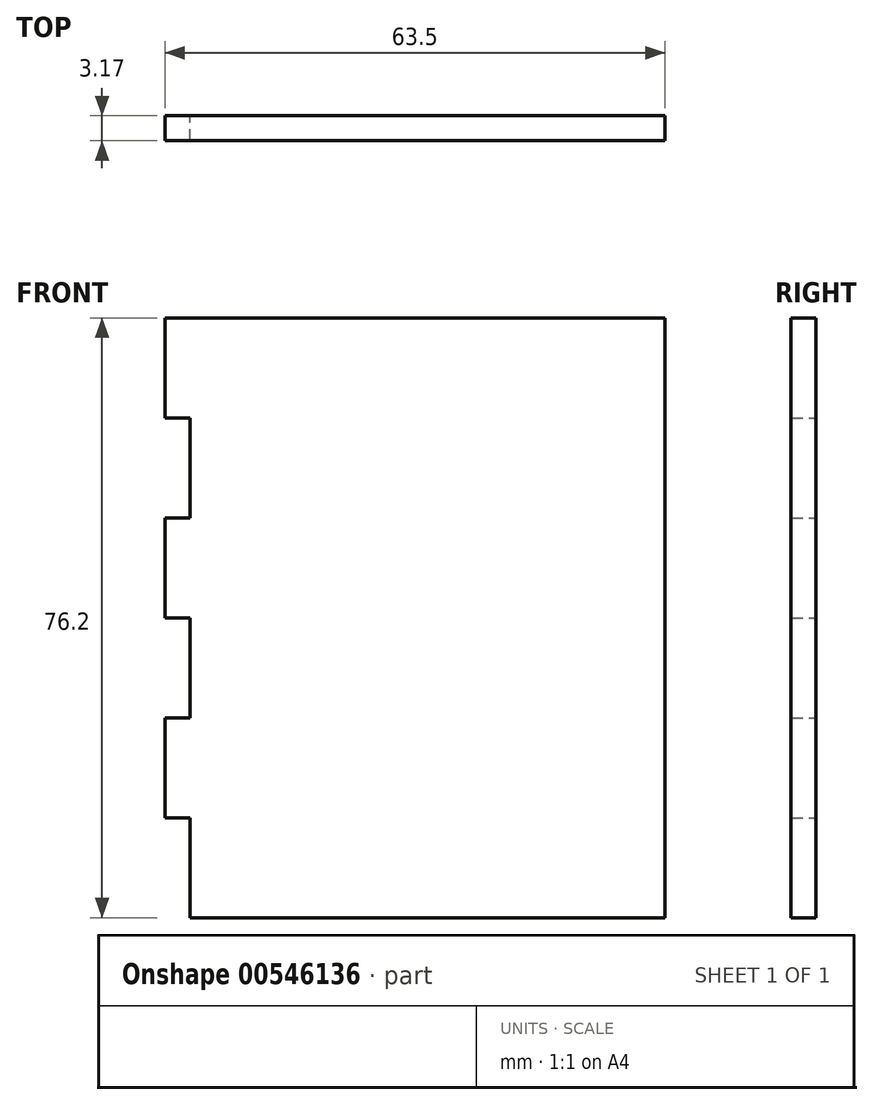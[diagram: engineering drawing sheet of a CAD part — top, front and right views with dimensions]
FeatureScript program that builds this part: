
annotation { "Feature Type Name" : "Feature", "Feature Type Description" : "" }
export const myFeature = defineFeature(function(context is Context, id is Id, definition is map)
    precondition{}
    {
        {
            var Q0;
            Q0=qCreatedBy(makeId("Front.planeOp"),FACE);
            var sketch = newSketch(context, id + "F0", { "sketchPlane" : qUnion([Q0])});
            skLineSegment(sketch, "E0.bottom", {"start": v(31.75, -38.1) * mm, "end": v(-31.75, -38.1) * mm});
            skLineSegment(sketch, "E0.top", {"start": v(31.75, 38.1) * mm, "end": v(-31.75, 38.1) * mm});
            skLineSegment(sketch, "E0.left", {"start": v(31.75, -38.1) * mm, "end": v(31.75, 38.1) * mm});
            skLineSegment(sketch, "E0.right", {"start": v(-31.75, -38.1) * mm, "end": v(-31.75, 38.1) * mm});
            skPoint(sketch, "E0.middle", {"position": v(0, 0) * mm});
            skSolve(sketch);
        }
        {
            var Q0;
            Q0 = qSketchRegion(id + "F0", true);
            extrude(context, id + "F1", {"entities" : qUnion([Q0]), "depth" : 3.17 * mm, "offsetDistance" : 25.4 * mm});
        }
        {
            var Q0;
            Q0=qCreatedBy(makeId("Front.planeOp"),FACE);
            var sketch = newSketch(context, id + "F2", { "sketchPlane" : qUnion([Q0])});
            skLineSegment(sketch, "E1.bottom", {"start": v(-31.75, 25.4) * mm, "end": v(-28.57, 25.4) * mm});
            skLineSegment(sketch, "E1.top", {"start": v(-31.75, 12.7) * mm, "end": v(-28.57, 12.7) * mm});
            skLineSegment(sketch, "E1.left", {"start": v(-31.75, 25.4) * mm, "end": v(-31.75, 12.7) * mm});
            skLineSegment(sketch, "E1.right", {"start": v(-28.57, 25.4) * mm, "end": v(-28.57, 12.7) * mm});
            skLineSegment(sketch, "E2.bottom", {"start": v(-31.75, 0) * mm, "end": v(-28.58, 0) * mm});
            skLineSegment(sketch, "E2.top", {"start": v(-31.75, -12.7) * mm, "end": v(-28.58, -12.7) * mm});
            skLineSegment(sketch, "E2.left", {"start": v(-31.75, 0) * mm, "end": v(-31.75, -12.7) * mm});
            skLineSegment(sketch, "E2.right", {"start": v(-28.58, 0) * mm, "end": v(-28.58, -12.7) * mm});
            skLineSegment(sketch, "E3.bottom", {"start": v(-28.58, -25.4) * mm, "end": v(-31.75, -25.4) * mm});
            skLineSegment(sketch, "E3.top", {"start": v(-28.58, -38.1) * mm, "end": v(-31.75, -38.1) * mm});
            skLineSegment(sketch, "E3.left", {"start": v(-28.58, -25.4) * mm, "end": v(-28.58, -38.1) * mm});
            skLineSegment(sketch, "E3.right", {"start": v(-31.75, -25.4) * mm, "end": v(-31.75, -38.1) * mm});
            skSolve(sketch);
        }
        {
            var Q0;
            Q0 = qSketchRegion(id + "F2", true);
            extrude(context, id + "F3", {"entities" : qUnion([Q0]), "operationType" : NewBodyOperationType.REMOVE, "endBound" : BoundingType.THROUGH_ALL, "depth" : 25.4 * mm, "offsetDistance" : 25.4 * mm});
        }
    });
